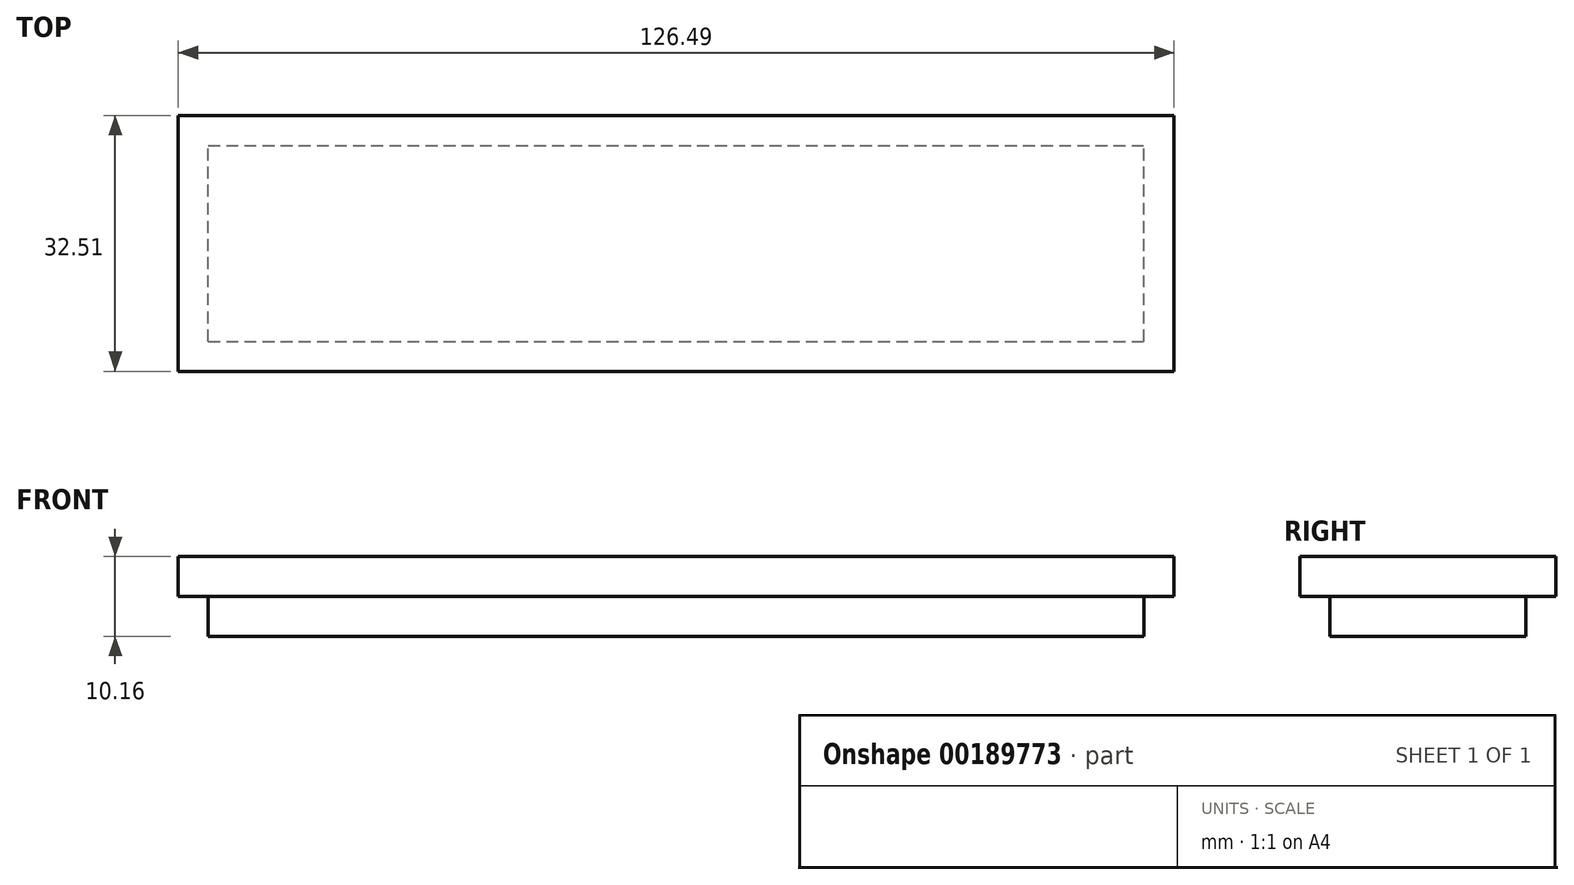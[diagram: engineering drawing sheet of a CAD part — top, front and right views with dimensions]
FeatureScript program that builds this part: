
annotation { "Feature Type Name" : "Feature", "Feature Type Description" : "" }
export const myFeature = defineFeature(function(context is Context, id is Id, definition is map)
    precondition{}
    {
        {
            var Q0;
            Q0=qCreatedBy(makeId("Top.planeOp"),FACE);
            var sketch = newSketch(context, id + "F0", { "sketchPlane" : qUnion([Q0])});
            skLineSegment(sketch, "E0.bottom", {"start": v(0, 0) * mm, "end": v(118.87, 0) * mm});
            skLineSegment(sketch, "E0.top", {"start": v(0, 24.9) * mm, "end": v(118.87, 24.9) * mm});
            skLineSegment(sketch, "E0.left", {"start": v(0, 0) * mm, "end": v(0, 24.9) * mm});
            skLineSegment(sketch, "E0.right", {"start": v(118.87, 0) * mm, "end": v(118.87, 24.9) * mm});
            skSolve(sketch);
        }
        {
            var Q0;
            Q0=makeQuery(id+"F0.imprint","IMPRINT",FACE,{"disambiguationData":[TD([[makeQuery(id+"F0.imprint","IMPRINT",EDGE,{"derivedFrom":sQuery(id+"F0.wireOp",EDGE,"E0.bottom")}),1.0]])]});
            extrude(context, id + "F1", {"entities" : qUnion([Q0]), "depth" : 5.08 * mm});
        }
        {
            var Q0;
            Q0=makeQuery(id+"F1.opExtrude","CAP_FACE",FACE,{"disambiguationData":[OSD([sQuery(id+"F0.wireOp",EDGE,"E0.bottom"),sQuery(id+"F0.wireOp",EDGE,"E0.top"),sQuery(id+"F0.wireOp",EDGE,"E0.left"),sQuery(id+"F0.wireOp",EDGE,"E0.right")])],"isStart":false});
            var sketch = newSketch(context, id + "F2", { "sketchPlane" : qUnion([Q0])});
            skLineSegment(sketch, "E1.bottom", {"start": v(-3.81, 28.7) * mm, "end": v(122.68, 28.7) * mm});
            skLineSegment(sketch, "E1.top", {"start": v(-3.81, -3.81) * mm, "end": v(122.68, -3.81) * mm});
            skLineSegment(sketch, "E1.left", {"start": v(-3.81, 28.7) * mm, "end": v(-3.8, -3.81) * mm});
            skLineSegment(sketch, "E1.right", {"start": v(122.68, 28.7) * mm, "end": v(122.68, -3.81) * mm});
            skSolve(sketch);
        }
        {
            var Q0;
            Q0=makeQuery(id+"F2.imprint","IMPRINT",FACE,{"disambiguationData":[TD([[makeQuery(id+"F2.imprint","IMPRINT",EDGE,{"derivedFrom":sQuery(id+"F2.wireOp",EDGE,"E1.bottom")}),-1.0]])]});
            var Q1;
            Q1=makeQuery(id+"F2.imprint","IMPRINT",FACE,{"disambiguationData":[TD([[makeQuery(id+"F2.imprint","IMPRINT",EDGE,{"derivedFrom":makeQuery(id+"F1.opExtrude","CAP_EDGE",EDGE,{"disambiguationData":[OSD([sQuery(id+"F0.wireOp",EDGE,"E0.bottom")])],"isStart":false})}),1.0]])]});
            extrude(context, id + "F3", {"entities" : qUnion([Q0, Q1]), "operationType" : NewBodyOperationType.ADD, "depth" : 5.08 * mm});
        }
    });
